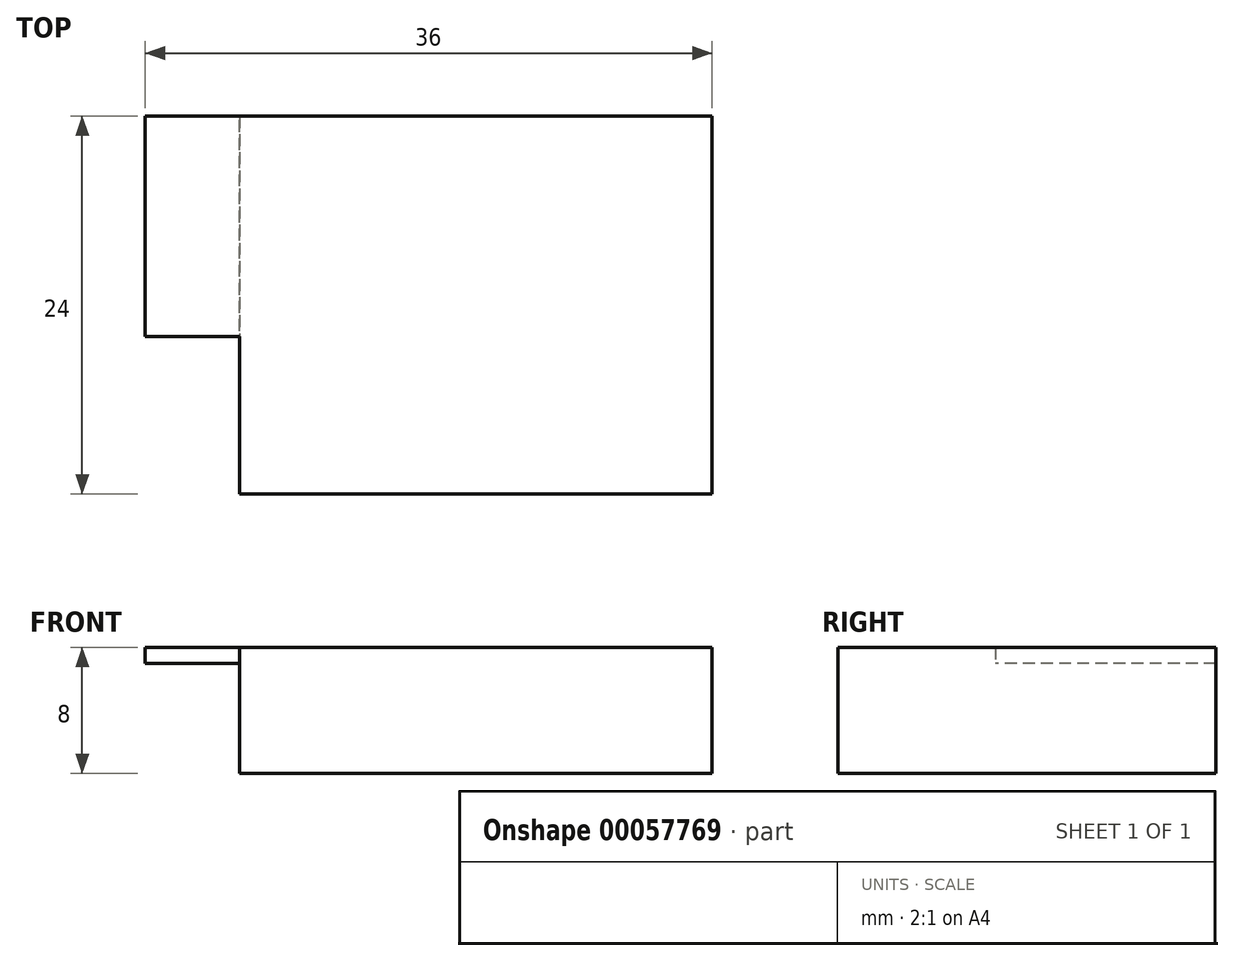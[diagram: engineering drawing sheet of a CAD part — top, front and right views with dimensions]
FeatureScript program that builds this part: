
annotation { "Feature Type Name" : "Feature", "Feature Type Description" : "" }
export const myFeature = defineFeature(function(context is Context, id is Id, definition is map)
    precondition{}
    {
        {
            var Q0;
            Q0=qCreatedBy(makeId("Top.planeOp"),FACE);
            var sketch = newSketch(context, id + "F0", { "sketchPlane" : qUnion([Q0])});
            skLineSegment(sketch, "E0.rect.bottom", {"start": v(15, -12) * mm, "end": v(-15, -12) * mm});
            skLineSegment(sketch, "E0.rect.top", {"start": v(15, 12) * mm, "end": v(-15, 12) * mm});
            skLineSegment(sketch, "E0.rect.left", {"start": v(15, -12) * mm, "end": v(15, 12) * mm});
            skLineSegment(sketch, "E0.rect.right", {"start": v(-15, -12) * mm, "end": v(-15, 12) * mm});
            skPoint(sketch, "E0.rect.middle", {"position": v(0, 0) * mm});
            skSolve(sketch);
        }
        {
            var Q0;
            Q0=makeQuery(id+"F0.imprint","IMPRINT",FACE,{"disambiguationData":[TD([[makeQuery(id+"F0.imprint","IMPRINT",EDGE,{"derivedFrom":sQuery(id+"F0.wireOp",EDGE,"E0.rect.bottom")}),-1.0]])]});
            extrude(context, id + "F1", {"entities" : qUnion([Q0]), "depth" : 8 * mm});
        }
        {
            var Q0;
            Q0=makeQuery(id+"F1.opExtrude","SWEPT_FACE",FACE,{"disambiguationData":[OSD([sQuery(id+"F0.wireOp",EDGE,"E0.rect.right")])]});
            var sketch = newSketch(context, id + "F2", { "sketchPlane" : qUnion([Q0])});
            skLineSegment(sketch, "E1.bottom", {"start": v(-12, 8) * mm, "end": v(2, 8) * mm});
            skLineSegment(sketch, "E1.top", {"start": v(-12, 7) * mm, "end": v(2, 7) * mm});
            skLineSegment(sketch, "E1.left", {"start": v(-12, 8) * mm, "end": v(-12, 7) * mm});
            skLineSegment(sketch, "E1.right", {"start": v(2, 8) * mm, "end": v(2, 7) * mm});
            skSolve(sketch);
        }
        {
            var Q0;
            Q0=makeQuery(id+"F2.imprint","IMPRINT",FACE,{"disambiguationData":[TD([[makeQuery(id+"F2.imprint","IMPRINT",EDGE,{"derivedFrom":sQuery(id+"F2.wireOp",EDGE,"E1.bottom")}),1.0]])]});
            extrude(context, id + "F3", {"entities" : qUnion([Q0]), "operationType" : NewBodyOperationType.ADD, "depth" : 6 * mm});
        }
    });
